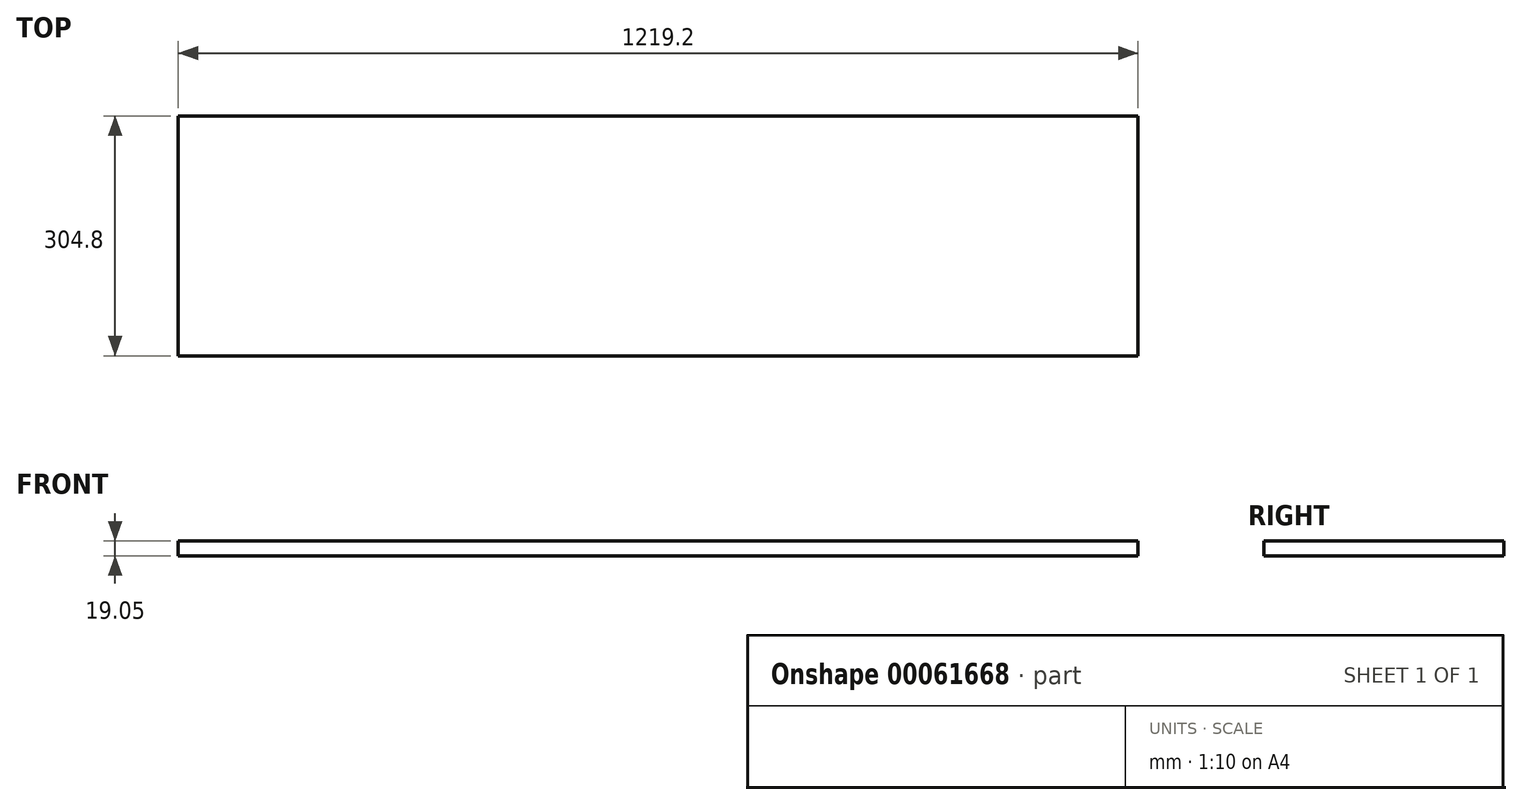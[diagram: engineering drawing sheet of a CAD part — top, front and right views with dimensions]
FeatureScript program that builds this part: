
annotation { "Feature Type Name" : "Feature", "Feature Type Description" : "" }
export const myFeature = defineFeature(function(context is Context, id is Id, definition is map)
    precondition{}
    {
        {
            var Q0;
            Q0=qCreatedBy(makeId("Top.planeOp"),FACE);
            var sketch = newSketch(context, id + "F0", { "sketchPlane" : qUnion([Q0])});
            skLineSegment(sketch, "E0.bottom", {"start": v(0, 0) * mm, "end": v(1219.2, 0) * mm});
            skLineSegment(sketch, "E0.top", {"start": v(0, 304.8) * mm, "end": v(1219.2, 304.8) * mm});
            skLineSegment(sketch, "E0.left", {"start": v(0, 0) * mm, "end": v(0, 304.8) * mm});
            skLineSegment(sketch, "E0.right", {"start": v(1219.2, 0) * mm, "end": v(1219.2, 304.8) * mm});
            skSolve(sketch);
        }
        {
            var Q0;
            Q0=makeQuery(id+"F0.imprint","IMPRINT",FACE,{"disambiguationData":[TD([[makeQuery(id+"F0.imprint","IMPRINT",EDGE,{"derivedFrom":sQuery(id+"F0.wireOp",EDGE,"E0.bottom")}),1.0]])]});
            extrude(context, id + "F1", {"entities" : qUnion([Q0]), "depth" : 19.05 * mm});
        }
    });
